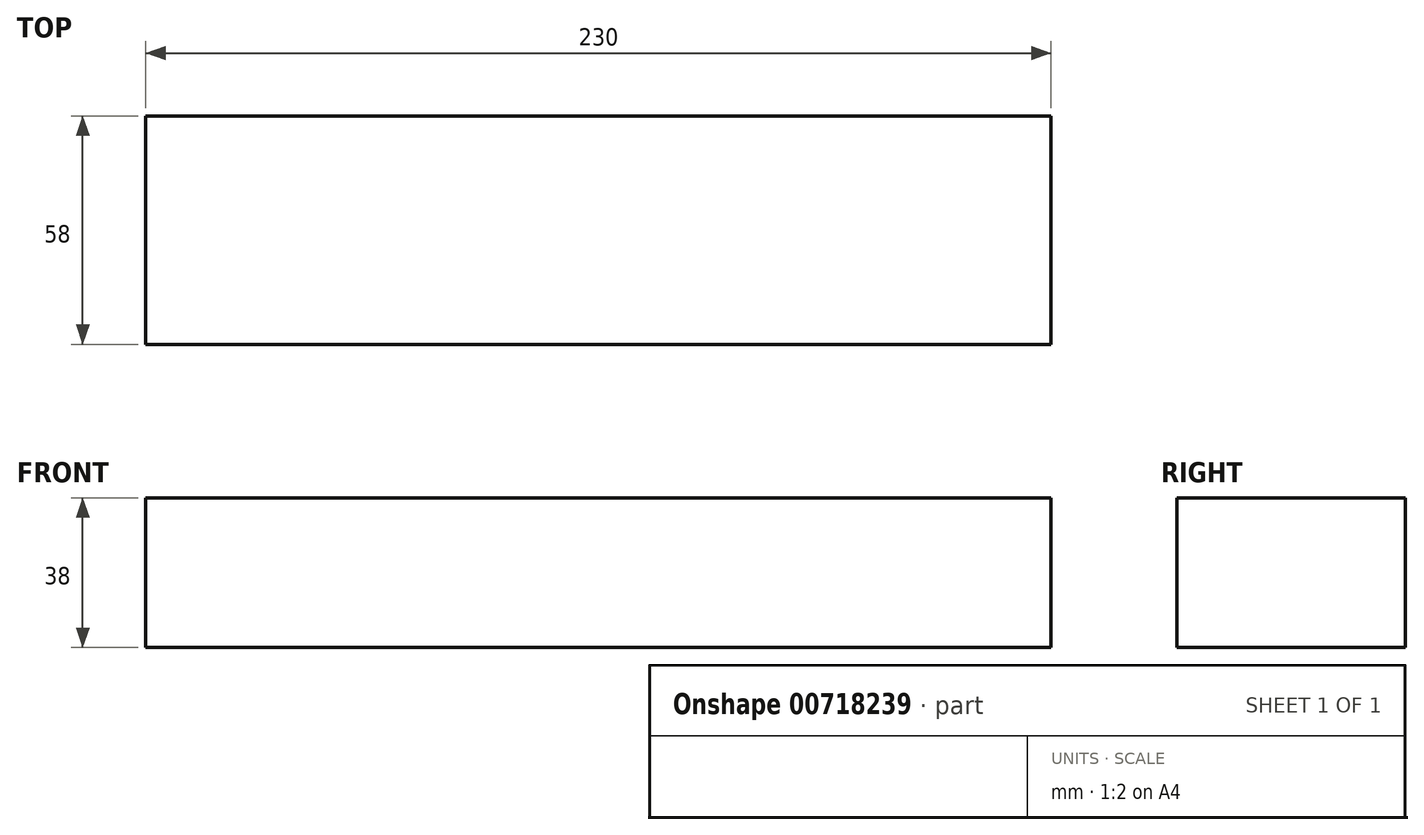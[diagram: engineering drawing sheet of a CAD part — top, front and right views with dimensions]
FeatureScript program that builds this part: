
annotation { "Feature Type Name" : "Feature", "Feature Type Description" : "" }
export const myFeature = defineFeature(function(context is Context, id is Id, definition is map)
    precondition{}
    {
        {
            var Q0;
            Q0=qCreatedBy(makeId("Front.planeOp"),FACE);
            var sketch = newSketch(context, id + "F0", { "sketchPlane" : qUnion([Q0])});
            skLineSegment(sketch, "E0.bottom", {"start": v(115, 19) * mm, "end": v(-115, 19) * mm});
            skLineSegment(sketch, "E0.top", {"start": v(115, -19) * mm, "end": v(-115, -19) * mm});
            skLineSegment(sketch, "E0.left", {"start": v(115, 19) * mm, "end": v(115, -19) * mm});
            skLineSegment(sketch, "E0.right", {"start": v(-115, 19) * mm, "end": v(-115, -19) * mm});
            skPoint(sketch, "E0.middle", {"position": v(0, 0) * mm});
            skSolve(sketch);
        }
        {
            var Q0;
            Q0=qSketchRegion(id+"F0",true);
            extrude(context, id + "F1", {"entities" : qUnion([Q0]), "depth" : 58 * mm, "offsetDistance" : 25 * mm});
        }
    });
